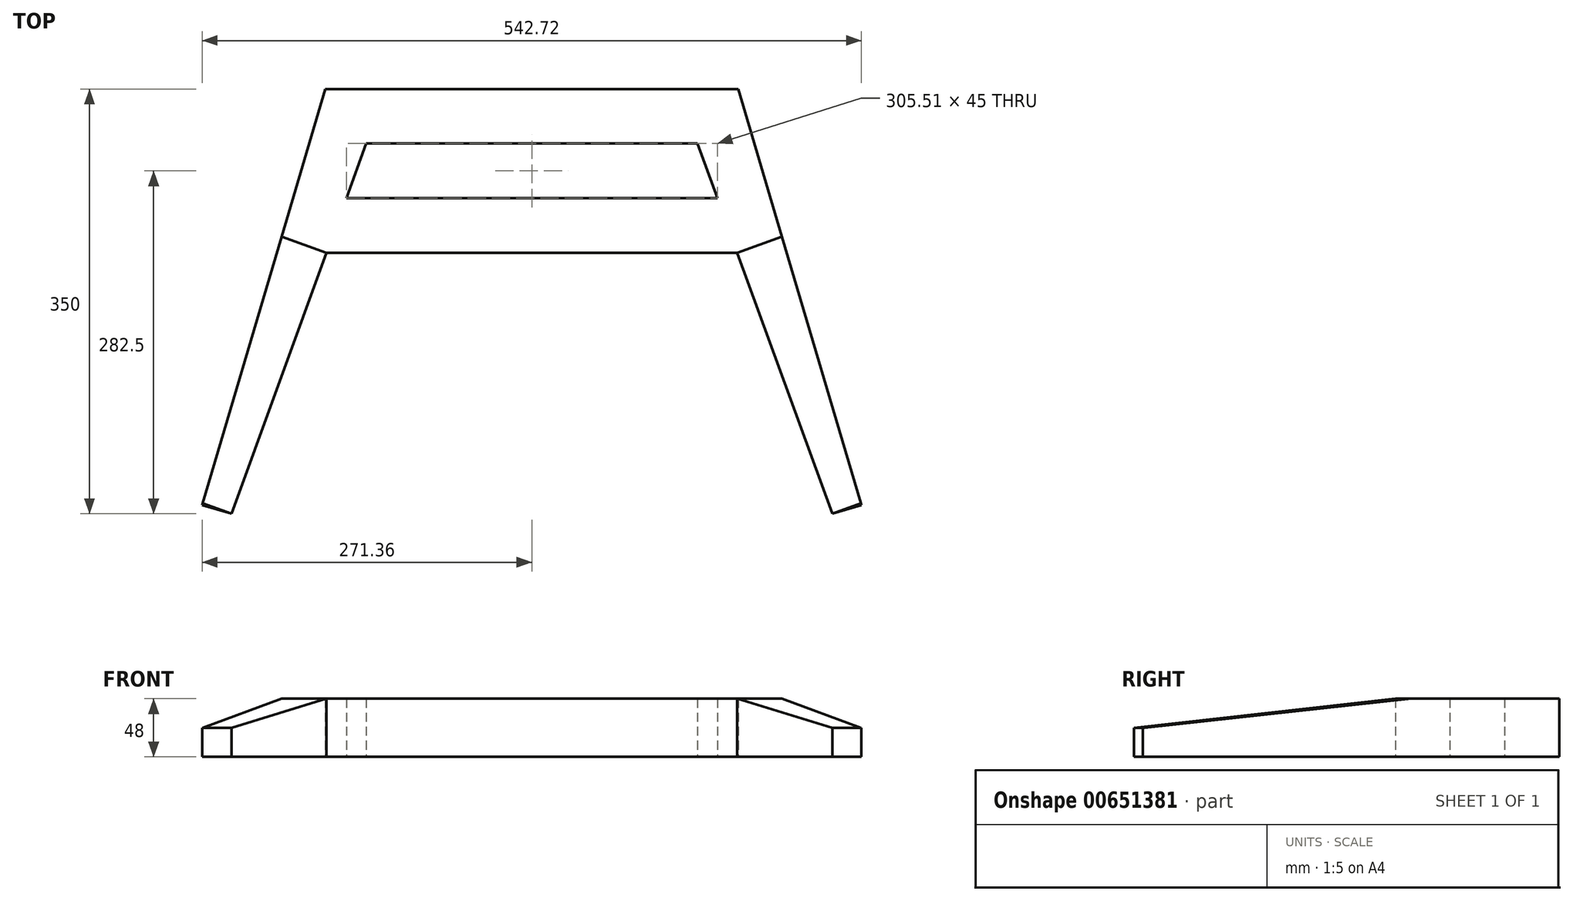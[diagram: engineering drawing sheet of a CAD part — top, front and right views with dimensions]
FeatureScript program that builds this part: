
annotation { "Feature Type Name" : "Feature", "Feature Type Description" : "" }
export const myFeature = defineFeature(function(context is Context, id is Id, definition is map)
    precondition{}
    {
        {
            var Q0;
            Q0=qCreatedBy(makeId("Top.planeOp"),FACE);
            var sketch = newSketch(context, id + "F0", { "sketchPlane" : qUnion([Q0])});
            skLineSegment(sketch, "E0", {"start": v(0, -293.09) * mm, "end": v(0, 393.92) * mm, "construction": true});
            skLineSegment(sketch, "E1", {"start": v(0, 135) * mm, "end": v(-170, 135) * mm});
            skLineSegment(sketch, "E2", {"start": v(-170, 135) * mm, "end": v(-271.36, -207.91) * mm});
            skLineSegment(sketch, "E3", {"start": v(-271.36, -207.91) * mm, "end": v(-247.39, -215) * mm});
            skLineSegment(sketch, "E4", {"start": v(-247.39, -215) * mm, "end": v(-136.38, 90) * mm});
            skLineSegment(sketch, "E5", {"start": v(-136.38, 90) * mm, "end": v(0, 90) * mm});
            skLineSegment(sketch, "E6", {"start": v(0, 90) * mm, "end": v(0, 135) * mm});
            skLineSegment(sketch, "E7", {"start": v(0, 45) * mm, "end": v(-152.76, 45) * mm});
            skLineSegment(sketch, "E8", {"start": v(-152.76, 45) * mm, "end": v(-169.13, 0) * mm});
            skLineSegment(sketch, "E9", {"start": v(-169.13, 0) * mm, "end": v(0, 0) * mm});
            skLineSegment(sketch, "E10", {"start": v(0, 0) * mm, "end": v(0, 45) * mm});
            skSolve(sketch);
        }
        {
            var Q0;
            Q0=makeQuery(id+"F0.imprint","IMPRINT",FACE,{"disambiguationData":[TD([[makeQuery(id+"F0.imprint","IMPRINT",EDGE,{"derivedFrom":sQuery(id+"F0.wireOp",EDGE,"E7")}),1.0]])]});
            var Q1;
            Q1=makeQuery(id+"F0.imprint","IMPRINT",FACE,{"disambiguationData":[TD([[makeQuery(id+"F0.imprint","IMPRINT",EDGE,{"derivedFrom":sQuery(id+"F0.wireOp",EDGE,"E1")}),1.0]])]});
            extrude(context, id + "F1", {"entities" : qUnion([Q0, Q1]), "depth" : 48 * mm, "offsetDistance" : 25 * mm});
        }
        {
            var Q0;
            {var subQ0=sQuery(id+"F0.wireOp",EDGE,"E4");Q0=makeQuery(id+"F1.opExtrude","SWEPT_FACE",FACE,{"disambiguationData":[OSD([subQ0]),TDD([makeQuery(id+"F0.imprint","IMPRINT",EDGE,{"disambiguationData":[TD([[makeQuery(id+"F0.imprint","INTERSECT",VERTEX,{"derivedFrom":[sQuery(id+"F0.wireOp",EDGE,"E3"),subQ0]}),-1.0]])],"derivedFrom":subQ0})])]});}
            var sketch = newSketch(context, id + "F2", { "sketchPlane" : qUnion([Q0])});
            skLineSegment(sketch, "E11", {"start": v(-57.85, 48) * mm, "end": v(-286.65, 24) * mm});
            skLineSegment(sketch, "E12", {"start": v(-286.65, 24) * mm, "end": v(-286.65, 48) * mm});
            skLineSegment(sketch, "E13", {"start": v(-286.65, 48) * mm, "end": v(-57.85, 48) * mm});
            skLineSegment(sketch, "E14", {"start": v(-286.65, 24) * mm, "end": v(-306.84, 24) * mm});
            skLineSegment(sketch, "E15", {"start": v(-286.65, 48) * mm, "end": v(-315.66, 48) * mm});
            skLineSegment(sketch, "E16", {"start": v(-315.66, 48) * mm, "end": v(-306.84, 24) * mm});
            skSolve(sketch);
        }
        {
            var Q0;
            Q0 = qSketchRegion(id + "F2", true);
            extrude(context, id + "F3", {"entities" : qUnion([Q0]), "operationType" : NewBodyOperationType.REMOVE, "endBound" : BoundingType.THROUGH_ALL, "oppositeDirection" : true, "depth" : 25 * mm, "offsetDistance" : 25 * mm});
        }
        {
            var Q0;
            Q0=makeQuery(id+"F1.opExtrude","SWEPT_BODY",BODY,{"disambiguationData":[OSD([sQuery(id+"F0.wireOp",EDGE,"E1"),sQuery(id+"F0.wireOp",EDGE,"E2"),sQuery(id+"F0.wireOp",EDGE,"E3"),sQuery(id+"F0.wireOp",EDGE,"E4"),sQuery(id+"F0.wireOp",EDGE,"E5"),sQuery(id+"F0.wireOp",EDGE,"E6"),sQuery(id+"F0.wireOp",EDGE,"E7"),sQuery(id+"F0.wireOp",EDGE,"E9"),sQuery(id+"F0.wireOp",EDGE,"E10")])]});
            var Q1;
            Q1=qCreatedBy(makeId("Right.planeOp"),FACE);
            mirror(context, id + "F4", {"operationType" : NewBodyOperationType.ADD, "entities" : qUnion([Q0]), "mirrorPlane" : qUnion([Q1])});
        }
    });
